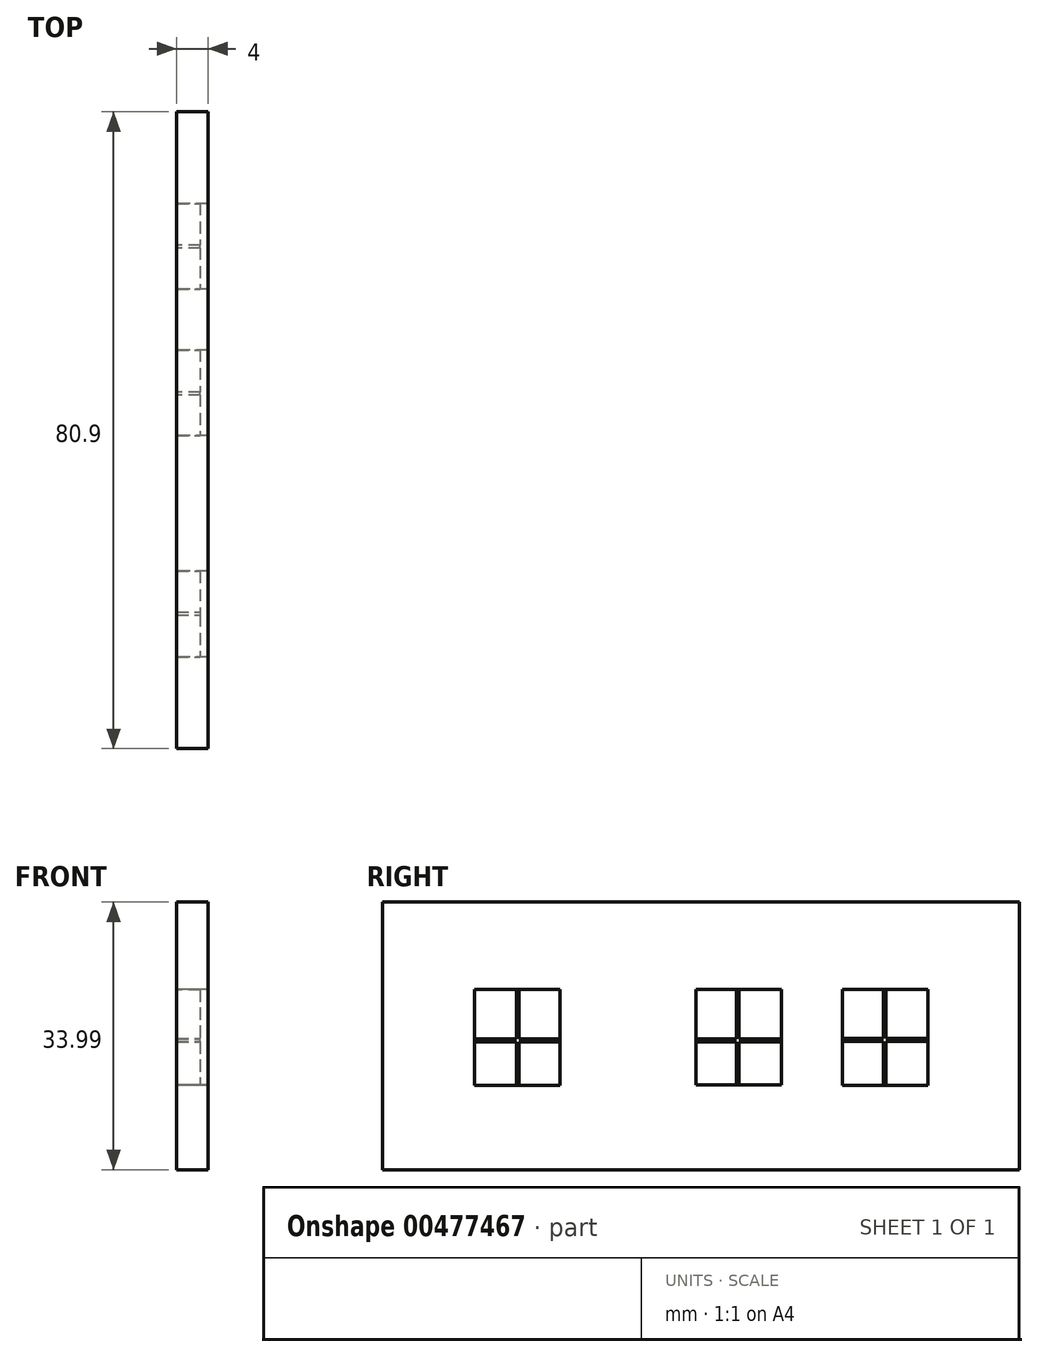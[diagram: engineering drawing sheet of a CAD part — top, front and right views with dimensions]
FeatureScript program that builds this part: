
annotation { "Feature Type Name" : "Feature", "Feature Type Description" : "" }
export const myFeature = defineFeature(function(context is Context, id is Id, definition is map)
    precondition{}
    {
        {
            var Q0;
            Q0=qCreatedBy(makeId("Right.planeOp"),FACE);
            var sketch = newSketch(context, id + "F0", { "sketchPlane" : qUnion([Q0])});
            skLineSegment(sketch, "E0.bottom", {"start": v(-42.27, 16.19) * mm, "end": v(38.63, 16.19) * mm});
            skLineSegment(sketch, "E0.top", {"start": v(-42.27, -17.8) * mm, "end": v(38.63, -17.8) * mm});
            skLineSegment(sketch, "E0.left", {"start": v(-42.27, 16.19) * mm, "end": v(-42.27, -17.8) * mm});
            skLineSegment(sketch, "E0.right", {"start": v(38.63, 16.19) * mm, "end": v(38.63, -17.8) * mm});
            skLineSegment(sketch, "E1.bottom", {"start": v(16.1, -7.07) * mm, "end": v(26.97, -7.07) * mm});
            skLineSegment(sketch, "E1.top", {"start": v(16.1, 5.1) * mm, "end": v(26.97, 5.1) * mm});
            skLineSegment(sketch, "E1.left", {"start": v(16.1, -7.07) * mm, "end": v(16.1, 5.1) * mm});
            skLineSegment(sketch, "E1.right", {"start": v(26.97, -7.07) * mm, "end": v(26.97, 5.1) * mm});
            skLineSegment(sketch, "E2.MirrorCS", {"start": v(-19.74, -7.07) * mm, "end": v(-30.61, -7.07) * mm});
            skLineSegment(sketch, "E3.MirrorCS", {"start": v(-19.74, -7.07) * mm, "end": v(-19.74, 5.1) * mm});
            skLineSegment(sketch, "E4.MirrorCS", {"start": v(-30.61, -7.07) * mm, "end": v(-30.61, 5.1) * mm});
            skLineSegment(sketch, "E5.MirrorCS", {"start": v(-19.74, 5.1) * mm, "end": v(-30.61, 5.1) * mm});
            skLineSegment(sketch, "E6.bottom", {"start": v(-2.5, -7.06) * mm, "end": v(8.38, -7.06) * mm});
            skLineSegment(sketch, "E6.top", {"start": v(-2.5, 5.1) * mm, "end": v(8.38, 5.1) * mm});
            skLineSegment(sketch, "E6.left", {"start": v(-2.5, -7.06) * mm, "end": v(-2.5, 5.1) * mm});
            skLineSegment(sketch, "E6.right", {"start": v(8.38, -7.06) * mm, "end": v(8.38, 5.1) * mm});
            skSolve(sketch);
        }
        {
            var Q0;
            Q0 = qSketchRegion(id + "F0", true);
            extrude(context, id + "F1", {"entities" : qUnion([Q0]), "depth" : 4 * mm});
        }
        {
            var Q0;
            Q0=qCreatedBy(makeId("Right.planeOp"),FACE);
            var sketch = newSketch(context, id + "F2", { "sketchPlane" : qUnion([Q0])});
            skLineSegment(sketch, "E7.bottom", {"start": v(-25.3, 5.02) * mm, "end": v(-24.94, 5.02) * mm});
            skLineSegment(sketch, "E7.top", {"start": v(-25.3, -7.2) * mm, "end": v(-24.94, -7.2) * mm});
            skLineSegment(sketch, "E7.left", {"start": v(-25.3, 5.02) * mm, "end": v(-25.3, -7.2) * mm});
            skLineSegment(sketch, "E7.right", {"start": v(-24.94, 5.02) * mm, "end": v(-24.94, -7.2) * mm});
            skLineSegment(sketch, "E8.bottom", {"start": v(2.65, 5.05) * mm, "end": v(3, 5.05) * mm});
            skLineSegment(sketch, "E8.top", {"start": v(2.65, -7.17) * mm, "end": v(3, -7.17) * mm});
            skLineSegment(sketch, "E8.left", {"start": v(2.65, 5.05) * mm, "end": v(2.65, -7.17) * mm});
            skLineSegment(sketch, "E8.right", {"start": v(3, 5.05) * mm, "end": v(3, -7.17) * mm});
            skLineSegment(sketch, "E9.bottom", {"start": v(21.32, 5.1) * mm, "end": v(21.67, 5.1) * mm});
            skLineSegment(sketch, "E9.top", {"start": v(21.32, -7.11) * mm, "end": v(21.67, -7.11) * mm});
            skLineSegment(sketch, "E9.left", {"start": v(21.32, 5.1) * mm, "end": v(21.32, -7.11) * mm});
            skLineSegment(sketch, "E9.right", {"start": v(21.67, 5.1) * mm, "end": v(21.67, -7.11) * mm});
            skLineSegment(sketch, "E10.bottom", {"start": v(27.58, -1.14) * mm, "end": v(27.58, -1.5) * mm});
            skLineSegment(sketch, "E10.top", {"start": v(15.36, -1.14) * mm, "end": v(15.36, -1.5) * mm});
            skLineSegment(sketch, "E10.left", {"start": v(27.58, -1.14) * mm, "end": v(15.36, -1.14) * mm});
            skLineSegment(sketch, "E10.right", {"start": v(27.58, -1.5) * mm, "end": v(15.36, -1.5) * mm});
            skLineSegment(sketch, "E11.bottom", {"start": v(9.32, -1.2) * mm, "end": v(9.32, -1.55) * mm});
            skLineSegment(sketch, "E11.top", {"start": v(-2.9, -1.2) * mm, "end": v(-2.9, -1.55) * mm});
            skLineSegment(sketch, "E11.left", {"start": v(9.32, -1.2) * mm, "end": v(-2.9, -1.2) * mm});
            skLineSegment(sketch, "E11.right", {"start": v(9.32, -1.55) * mm, "end": v(-2.9, -1.55) * mm});
            skLineSegment(sketch, "E12.bottom", {"start": v(-18.9, -1.22) * mm, "end": v(-18.9, -1.56) * mm});
            skLineSegment(sketch, "E12.top", {"start": v(-31.11, -1.22) * mm, "end": v(-31.11, -1.56) * mm});
            skLineSegment(sketch, "E12.left", {"start": v(-18.9, -1.22) * mm, "end": v(-31.11, -1.22) * mm});
            skLineSegment(sketch, "E12.right", {"start": v(-18.9, -1.56) * mm, "end": v(-31.11, -1.56) * mm});
            skSolve(sketch);
        }
        {
            var Q0;
            Q0 = qSketchRegion(id + "F2", true);
            extrude(context, id + "F3", {"entities" : qUnion([Q0]), "operationType" : NewBodyOperationType.ADD, "depth" : 3 * mm});
        }
    });
